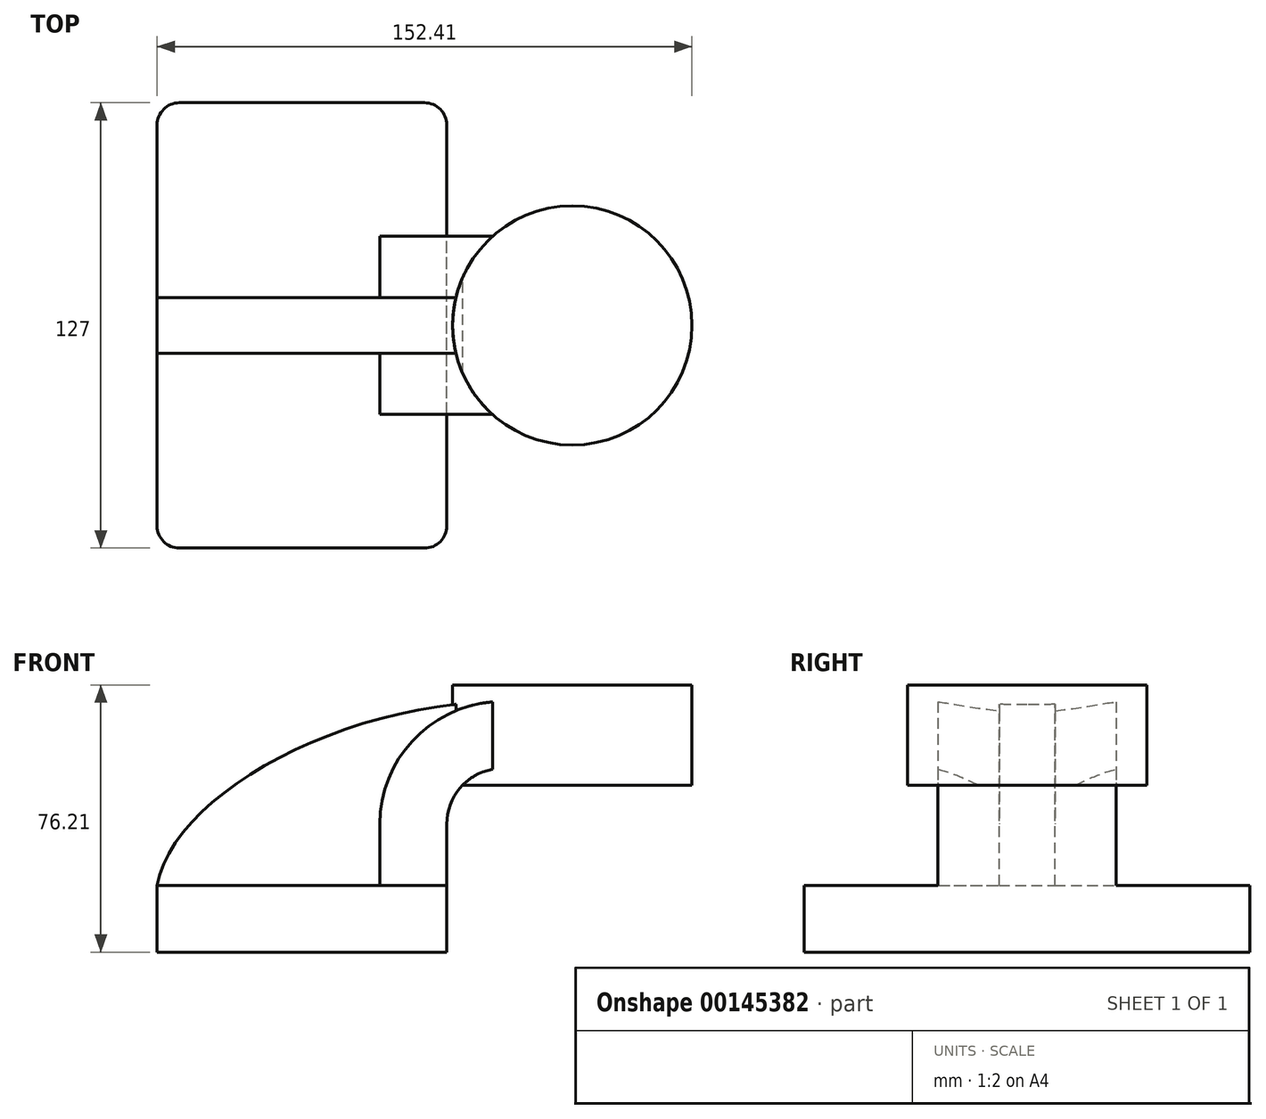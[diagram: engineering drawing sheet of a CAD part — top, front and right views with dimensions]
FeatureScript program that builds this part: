
annotation { "Feature Type Name" : "Feature", "Feature Type Description" : "" }
export const myFeature = defineFeature(function(context is Context, id is Id, definition is map)
    precondition{}
    {
        {
            var Q0;
            Q0=qCreatedBy(makeId("Front.planeOp"),FACE);
            var sketch = newSketch(context, id + "F0", { "sketchPlane" : qUnion([Q0])});
            skLineSegment(sketch, "E0.bottom", {"start": v(41.28, -9.52) * mm, "end": v(-41.28, -9.53) * mm});
            skLineSegment(sketch, "E0.top", {"start": v(41.28, 9.53) * mm, "end": v(-41.28, 9.53) * mm});
            skLineSegment(sketch, "E0.left", {"start": v(41.28, -9.52) * mm, "end": v(41.28, 9.53) * mm});
            skLineSegment(sketch, "E0.right", {"start": v(-41.28, -9.52) * mm, "end": v(-41.28, 9.53) * mm});
            skPoint(sketch, "E0.middle", {"position": v(0, 0) * mm});
            skLineSegment(sketch, "E1", {"start": v(41.28, 9.53) * mm, "end": v(41.28, 27) * mm});
            skArc(sketch, "E2", {"start": v(41.27, 27) * mm, "mid": v(45.92, 38.23) * mm, "end": v(57.15, 42.88) * mm});
            skLineSegment(sketch, "E3", {"start": v(57.15, 42.88) * mm, "end": v(77.03, 42.88) * mm});
            skLineSegment(sketch, "E4.bottom", {"start": v(111.12, 38.1) * mm, "end": v(60.33, 38.1) * mm});
            skLineSegment(sketch, "E4.top", {"start": v(111.12, 66.68) * mm, "end": v(60.33, 66.68) * mm});
            skLineSegment(sketch, "E4.left", {"start": v(111.12, 38.1) * mm, "end": v(111.12, 66.68) * mm});
            skLineSegment(sketch, "E4.right", {"start": v(60.33, 38.1) * mm, "end": v(60.33, 66.68) * mm});
            skPoint(sketch, "E4.middle", {"position": v(85.72, 52.39) * mm});
            skLineSegment(sketch, "E5.0", {"start": v(57.15, 61.93) * mm, "end": v(77.03, 61.93) * mm});
            skArc(sketch, "E5.1", {"start": v(22.23, 27) * mm, "mid": v(32.45, 51.7) * mm, "end": v(57.15, 61.93) * mm});
            skLineSegment(sketch, "E5.2", {"start": v(22.23, 9.53) * mm, "end": v(22.23, 27) * mm});
            skLineSegment(sketch, "E6", {"start": v(77.03, 38.1) * mm, "end": v(77.03, 66.68) * mm});
            skFitSpline(sketch, "E7", {"points": [v(-41.28, 9.53) * mm, v(57.15, 61.93) * mm], "startDerivative": vector(14, 77.67) * mm, "endDerivative": vector(138.4, 1.13) * mm});
            skSolve(sketch);
        }
        {
            var Q0;
            Q0=makeQuery(id+"F0.imprint","IMPRINT",FACE,{"disambiguationData":[TD([[makeQuery(id+"F0.imprint","IMPRINT",EDGE,{"derivedFrom":sQuery(id+"F0.wireOp",EDGE,"E0.bottom")}),-1.0]])]});
            extrude(context, id + "F1", {"entities" : qUnion([Q0]), "endBound" : BoundingType.SYMMETRIC, "depth" : 127 * mm});
        }
        {
            var Q0;
            {var subQ9=sQuery(id+"F0.wireOp",EDGE,"E1");Q0=makeQuery(id+"F0.imprint","IMPRINT",FACE,{"disambiguationData":[TD([[makeQuery(id+"F0.imprint","IMPRINT",EDGE,{"derivedFrom":subQ9}),1.0]])]});}
            var Q1;
            {var subQ0=sQuery(id+"F0.wireOp",EDGE,"E6");var subQ1=sQuery(id+"F0.wireOp",EDGE,"E3");var subQ2=makeQuery(id+"F0.imprint","INTERSECT",VERTEX,{"derivedFrom":[subQ1,subQ0]});Q1=makeQuery(id+"F0.imprint","IMPRINT",FACE,{"disambiguationData":[TD([[makeQuery(id+"F0.imprint","IMPRINT",EDGE,{"disambiguationData":[TD([[subQ2,1.0]])],"derivedFrom":subQ1}),1.0]])]});}
            extrude(context, id + "F2", {"entities" : qUnion([Q0, Q1]), "operationType" : NewBodyOperationType.ADD, "endBound" : BoundingType.SYMMETRIC, "depth" : 50.8 * mm});
        }
        {
            var Q0;
            {var subQ3=sQuery(id+"F0.wireOp",EDGE,"E5.2");Q0=makeQuery(id+"F0.imprint","IMPRINT",FACE,{"disambiguationData":[TD([[makeQuery(id+"F0.imprint","IMPRINT",EDGE,{"derivedFrom":subQ3}),1.0]])]});}
            extrude(context, id + "F3", {"entities" : qUnion([Q0]), "operationType" : NewBodyOperationType.ADD, "endBound" : BoundingType.SYMMETRIC, "depth" : 15.88 * mm});
        }
        {
            var Q0;
            {var subQ4=sQuery(id+"F0.wireOp",EDGE,"E4.left");Q0=makeQuery(id+"F0.imprint","IMPRINT",FACE,{"disambiguationData":[TD([[makeQuery(id+"F0.imprint","IMPRINT",EDGE,{"derivedFrom":subQ4}),1.0]])]});}
            var Q1;
            Q1=sQuery(id+"F0.wireOp",EDGE,"E6");
            revolve(context, id + "F4", {"operationType" : NewBodyOperationType.ADD, "entities" : qUnion([Q0]), "axis" : qUnion([Q1]), "revolveType" : RevolveType.FULL});
        }
        {
            var Q0;
            Q0=makeQuery(id+"F1.opExtrude","CAP_EDGE",EDGE,{"disambiguationData":[OSD([sQuery(id+"F0.wireOp",EDGE,"E0.left")])],"isStart":false});
            var Q1;
            Q1=makeQuery(id+"F1.opExtrude","CAP_EDGE",EDGE,{"disambiguationData":[OSD([sQuery(id+"F0.wireOp",EDGE,"E0.right")])],"isStart":false});
            var Q2;
            Q2=makeQuery(id+"F1.opExtrude","CAP_EDGE",EDGE,{"disambiguationData":[OSD([sQuery(id+"F0.wireOp",EDGE,"E0.left")])],"isStart":true});
            var Q3;
            Q3=makeQuery(id+"F1.opExtrude","CAP_EDGE",EDGE,{"disambiguationData":[OSD([sQuery(id+"F0.wireOp",EDGE,"E0.right")])],"isStart":true});
            fillet(context, id + "F5", {"entities" : qUnion([Q0, Q1, Q2, Q3]), "radius" : 6.35 * mm, "tangentPropagation" : true, "allowEdgeOverflow" : false});
        }
    });
